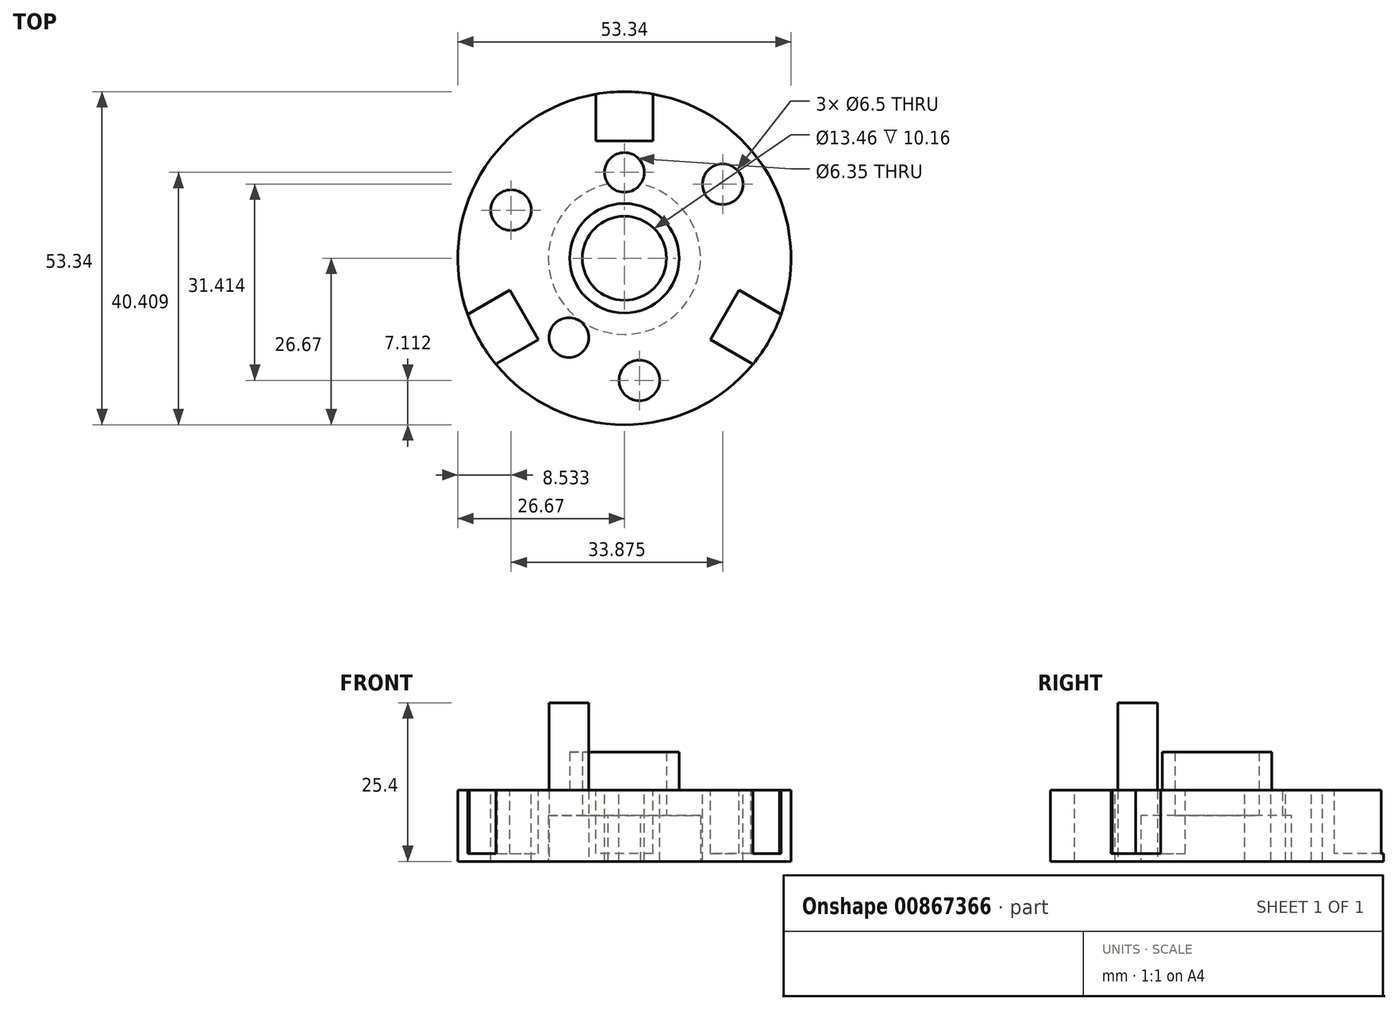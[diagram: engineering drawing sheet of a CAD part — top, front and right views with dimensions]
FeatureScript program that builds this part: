
annotation { "Feature Type Name" : "Feature", "Feature Type Description" : "" }
export const myFeature = defineFeature(function(context is Context, id is Id, definition is map)
    precondition{}
    {
        {
            var Q0;
            Q0=qCreatedBy(makeId("Top.planeOp"),FACE);
            var sketch = newSketch(context, id + "F0", { "sketchPlane" : qUnion([Q0])});
            skCircle(sketch, "E0", {"center": v(0, 0) * mm, "radius": 26.67 * mm});
            skSolve(sketch);
        }
        {
            var Q0;
            Q0 = qSketchRegion(id + "F0", true);
            extrude(context, id + "F1", {"entities" : qUnion([Q0]), "depth" : 11.43 * mm, "offsetDistance" : 25.4 * mm});
        }
        {
            var Q0;
            Q0=makeQuery(id+"F1.opExtrude","CAP_FACE",FACE,{"disambiguationData":[OSD([sQuery(id+"F0.wireOp",EDGE,"E0")])],"isStart":false});
            var sketch = newSketch(context, id + "F2", { "sketchPlane" : qUnion([Q0])});
            skCircle(sketch, "E1", {"center": v(0, 0) * mm, "radius": 8.76 * mm});
            skCircle(sketch, "E2", {"center": v(0, 0) * mm, "radius": 6.73 * mm});
            skSolve(sketch);
        }
        {
            var Q0;
            Q0 = qSketchRegion(id + "F2", true);
            extrude(context, id + "F3", {"entities" : qUnion([Q0]), "operationType" : NewBodyOperationType.ADD, "depth" : 6.1 * mm, "offsetDistance" : 25.4 * mm});
        }
        {
            var Q0;
            Q0=makeQuery(id+"F1.opExtrude","CAP_FACE",FACE,{"disambiguationData":[OSD([sQuery(id+"F0.wireOp",EDGE,"E0")])],"isStart":true});
            var sketch = newSketch(context, id + "F4", { "sketchPlane" : qUnion([Q0])});
            skCircle(sketch, "E3", {"center": v(0, 0) * mm, "radius": 29.21 * mm});
            skSolve(sketch);
        }
        {
            var Q0;
            Q0=makeQuery(id+"F4.imprint","IMPRINT",FACE,{"disambiguationData":[TD([[makeQuery(id+"F4.imprint","IMPRINT",EDGE,{"derivedFrom":sQuery(id+"F4.wireOp",EDGE,"E3")}),1.0]])]});
            var Q1;
            Q1=makeQuery(id+"F4.imprint","IMPRINT",FACE,{"disambiguationData":[TD([[makeQuery(id+"F4.imprint","IMPRINT",EDGE,{"derivedFrom":makeQuery(id+"F1.opExtrude","CAP_EDGE",EDGE,{"disambiguationData":[OSD([sQuery(id+"F0.wireOp",EDGE,"E0")])],"isStart":true})}),-1.0]])]});
            extrude(context, id + "F5", {"entities" : qUnion([Q0, Q1]), "depth" : 2.8 * mm, "offsetDistance" : 25.4 * mm});
        }
        {
            var Q0;
            Q0=qCreatedBy(makeId("Top.planeOp"),FACE);
            var sketch = newSketch(context, id + "F6", { "sketchPlane" : qUnion([Q0])});
            skCircle(sketch, "E4", {"center": v(0, 0) * mm, "radius": 6.73 * mm});
            skSolve(sketch);
        }
        {
            var Q0;
            Q0 = qSketchRegion(id + "F6", true);
            extrude(context, id + "F7", {"entities" : qUnion([Q0]), "operationType" : NewBodyOperationType.REMOVE, "depth" : 25.4 * mm, "offsetDistance" : 25.4 * mm});
        }
        {
            var Q0;
            Q0=makeQuery(id+"F5.opExtrude","CAP_FACE",FACE,{"disambiguationData":[OSD([sQuery(id+"F4.wireOp",EDGE,"E3")])],"isStart":false});
            var sketch = newSketch(context, id + "F8", { "sketchPlane" : qUnion([Q0])});
            skCircle(sketch, "E5", {"center": v(0, 0) * mm, "radius": 12.2 * mm});
            skSolve(sketch);
        }
        {
            var Q0;
            Q0 = qSketchRegion(id + "F8", true);
            extrude(context, id + "F9", {"entities" : qUnion([Q0]), "operationType" : NewBodyOperationType.REMOVE, "oppositeDirection" : true, "depth" : 10.16 * mm, "offsetDistance" : 25.4 * mm});
        }
        {
            var Q0;
            {var subQ0=sQuery(id+"F0.wireOp",EDGE,"E0");Q0=makeQuery(id+"F3.boolean.opBoolean","SPLIT",FACE,{"disambiguationData":[TD([makeQuery(id+"F1.opExtrude","SWEPT_FACE",FACE,{"disambiguationData":[OSD([subQ0])]})])],"derivedFrom":makeQuery(id+"F1.opExtrude","CAP_FACE",FACE,{"disambiguationData":[OSD([subQ0])],"isStart":false})});}
            var sketch = newSketch(context, id + "F10", { "sketchPlane" : qUnion([Q0])});
            skArc(sketch, "E6", {"start": v(4.56, 26.28) * mm, "mid": v(0, 31.24) * mm, "end": v(-4.56, 26.28) * mm});
            skLineSegment(sketch, "E7", {"start": v(4.56, 26.28) * mm, "end": v(4.56, 18.78) * mm});
            skLineSegment(sketch, "E8", {"start": v(4.56, 18.78) * mm, "end": v(-4.56, 18.78) * mm});
            skLineSegment(sketch, "E9", {"start": v(-4.56, 26.28) * mm, "end": v(-4.56, 18.78) * mm});
            skLineSegment(sketch, "E10.1.0", {"start": v(-20.29, -16.75) * mm, "end": v(-13.8, -13) * mm});
            skLineSegment(sketch, "E10.1.1", {"start": v(-24.84, -8.86) * mm, "end": v(-18.35, -5.12) * mm});
            skArc(sketch, "E10.1.2", {"start": v(-24.84, -8.86) * mm, "mid": v(-26.87, -15.3) * mm, "end": v(-20.29, -16.75) * mm});
            skLineSegment(sketch, "E10.1.3", {"start": v(-18.35, -5.12) * mm, "end": v(-13.8, -13) * mm});
            skLineSegment(sketch, "E10.2.0", {"start": v(24.84, -8.86) * mm, "end": v(18.35, -5.12) * mm});
            skLineSegment(sketch, "E10.2.1", {"start": v(20.29, -16.75) * mm, "end": v(13.8, -13) * mm});
            skArc(sketch, "E10.2.2", {"start": v(20.29, -16.75) * mm, "mid": v(26.87, -15.3) * mm, "end": v(24.84, -8.86) * mm});
            skLineSegment(sketch, "E10.2.3", {"start": v(13.8, -13) * mm, "end": v(18.35, -5.12) * mm});
            skPoint(sketch, "E10.center", {"position": v(0, 0.22) * mm});
            skSolve(sketch);
        }
        {
            var Q0;
            Q0 = qSketchRegion(id + "F10", true);
            extrude(context, id + "F11", {"entities" : qUnion([Q0]), "operationType" : NewBodyOperationType.REMOVE, "oppositeDirection" : true, "depth" : 10.16 * mm, "offsetDistance" : 25.4 * mm});
        }
        {
            var Q0;
            {var subQ0=sQuery(id+"F0.wireOp",EDGE,"E0");Q0=makeQuery(id+"F3.boolean.opBoolean","SPLIT",FACE,{"disambiguationData":[TD([makeQuery(id+"F1.opExtrude","SWEPT_FACE",FACE,{"disambiguationData":[OSD([subQ0])]})])],"derivedFrom":makeQuery(id+"F1.opExtrude","CAP_FACE",FACE,{"disambiguationData":[OSD([subQ0])],"isStart":false})});}
            var sketch = newSketch(context, id + "F12", { "sketchPlane" : qUnion([Q0])});
            skCircle(sketch, "E11", {"center": v(15.74, 11.86) * mm, "radius": 3.25 * mm});
            skCircle(sketch, "E12.1.0", {"center": v(-18.14, 7.7) * mm, "radius": 3.25 * mm});
            skCircle(sketch, "E12.2.0", {"center": v(2.4, -19.56) * mm, "radius": 3.25 * mm});
            skPoint(sketch, "E12.center", {"position": v(0, 0) * mm});
            skSolve(sketch);
        }
        {
            var Q0;
            Q0 = qSketchRegion(id + "F12", true);
            extrude(context, id + "F13", {"entities" : qUnion([Q0]), "operationType" : NewBodyOperationType.REMOVE, "oppositeDirection" : true, "depth" : 25.4 * mm, "offsetDistance" : 25.4 * mm});
        }
        {
            var Q0;
            Q0=qCreatedBy(makeId("Top.planeOp"),FACE);
            var sketch = newSketch(context, id + "F14", { "sketchPlane" : qUnion([Q0])});
            skCircle(sketch, "E13", {"center": v(-8.9, -12.7) * mm, "radius": 3.18 * mm});
            skSolve(sketch);
        }
        {
            var Q0;
            Q0 = qSketchRegion(id + "F14", true);
            extrude(context, id + "F15", {"entities" : qUnion([Q0]), "depth" : 25.4 * mm, "offsetDistance" : 25.4 * mm});
        }
        {
            var Q0;
            {var subQ0=sQuery(id+"F0.wireOp",EDGE,"E0");Q0=makeQuery(id+"F3.boolean.opBoolean","SPLIT",FACE,{"disambiguationData":[TD([makeQuery(id+"F1.opExtrude","SWEPT_FACE",FACE,{"disambiguationData":[OSD([subQ0])]})])],"derivedFrom":makeQuery(id+"F1.opExtrude","CAP_FACE",FACE,{"disambiguationData":[OSD([subQ0])],"isStart":false})});}
            var sketch = newSketch(context, id + "F16", { "sketchPlane" : qUnion([Q0])});
            skCircle(sketch, "E14", {"center": v(0, 13.74) * mm, "radius": 3.18 * mm});
            skSolve(sketch);
        }
        {
            var Q0;
            Q0 = qSketchRegion(id + "F16", true);
            var Q1;
            Q1=makeQuery(id+"F5.opExtrude","CAP_FACE",FACE,{"disambiguationData":[OSD([sQuery(id+"F4.wireOp",EDGE,"E3")])],"isStart":true});
            var Q2;
            Q2=makeQuery(id+"F5.opExtrude","CAP_FACE",FACE,{"disambiguationData":[OSD([sQuery(id+"F4.wireOp",EDGE,"E3")])],"isStart":false});
            extrude(context, id + "F17", {"entities" : qUnion([Q0, Q1, Q2]), "operationType" : NewBodyOperationType.REMOVE, "oppositeDirection" : true, "depth" : 50.8 * mm, "offsetDistance" : 25.4 * mm});
        }
    });
